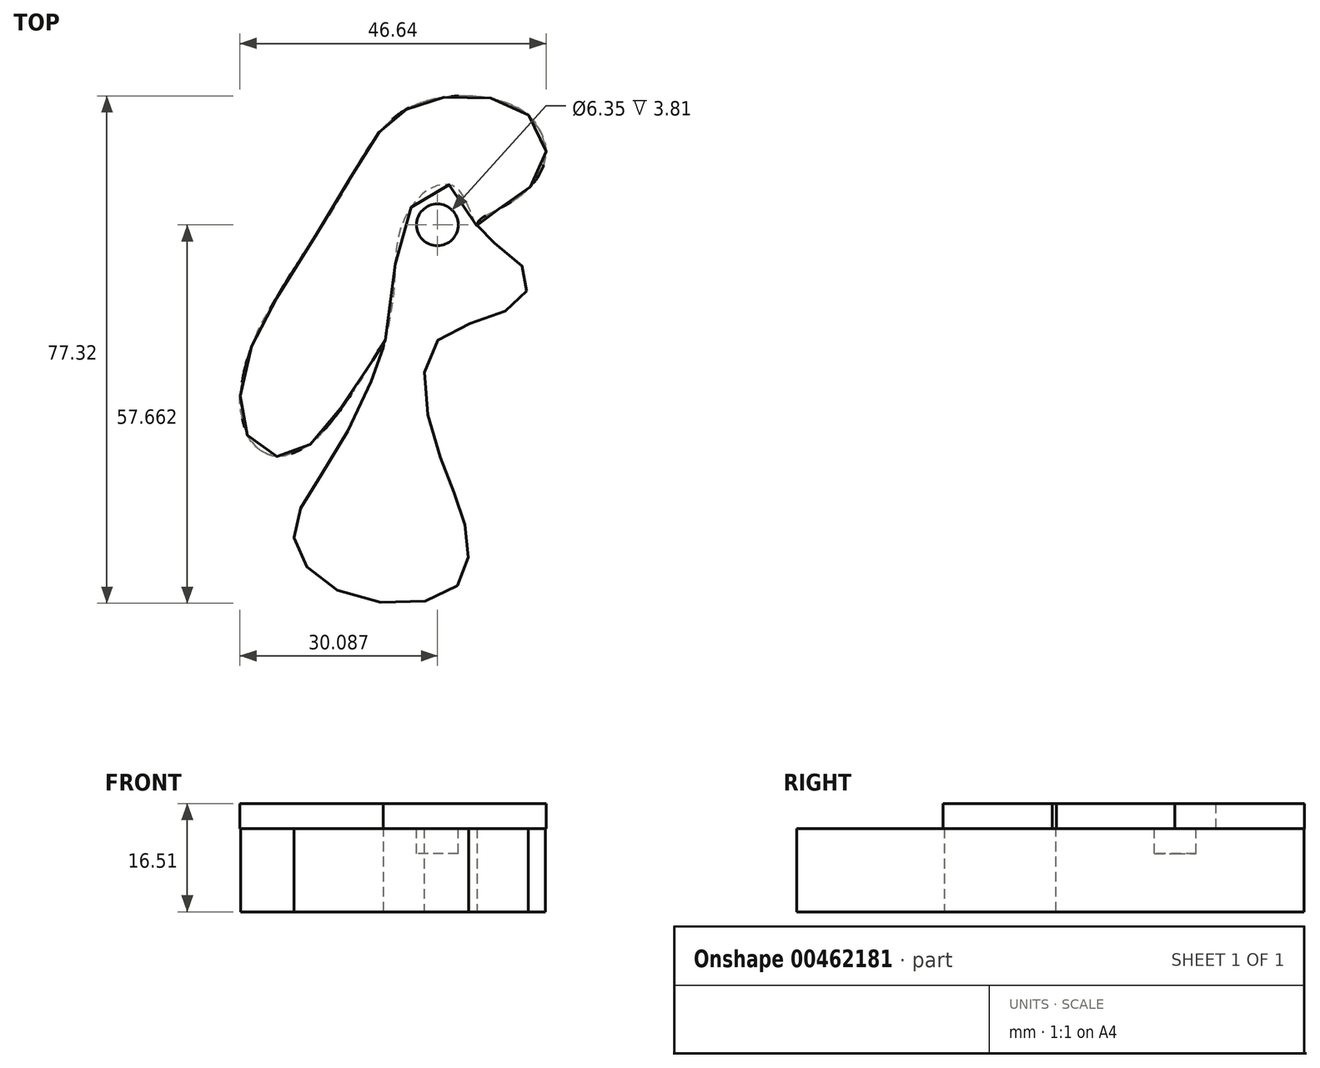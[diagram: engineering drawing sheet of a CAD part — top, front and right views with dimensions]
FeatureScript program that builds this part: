
annotation { "Feature Type Name" : "Feature", "Feature Type Description" : "" }
export const myFeature = defineFeature(function(context is Context, id is Id, definition is map)
    precondition{}
    {
        {
            var Q0;
            Q0=qCreatedBy(makeId("Top.planeOp"),FACE);
            var sketch = newSketch(context, id + "F0", { "sketchPlane" : qUnion([Q0])});
            skFitSpline(sketch, "E0", {"points": [v(0, 0) * mm, v(-6.4, -15.12) * mm, v(-13.6, -28.84) * mm, v(-6.63, -37.68) * mm, v(10.58, -37.45) * mm, v(12.68, -28.6) * mm, v(8.26, -16.05) * mm, v(7.8, 0) * mm, v(19.65, 5.58) * mm, v(21.51, 11.4) * mm, v(14.3, 17.9) * mm, v(18.72, 21.17) * mm, v(24.54, 27.68) * mm, v(21.05, 35.59) * mm, v(4.07, 36.05) * mm, v(-6.86, 21.86) * mm, v(-20.82, -2.8) * mm, v(-19.42, -15.58) * mm, v(-10.82, -14.89) * mm, v(0, 0) * mm]});
            skSolve(sketch);
        }
        {
            var Q0;
            Q0=makeQuery(id+"F0.imprint","IMPRINT",FACE,{"disambiguationData":[TD([[makeQuery(id+"F0.imprint","IMPRINT",EDGE,{"derivedFrom":sQuery(id+"F0.wireOp",EDGE,"E0")}),1.0]])]});
            extrude(context, id + "F1", {"entities" : qUnion([Q0]), "depth" : 12.7 * mm});
        }
        {
            var Q0;
            Q0=makeQuery(id+"F1.opExtrude","CAP_FACE",FACE,{"disambiguationData":[OSD([sQuery(id+"F0.wireOp",EDGE,"E0")])],"isStart":false});
            var sketch = newSketch(context, id + "F2", { "sketchPlane" : qUnion([Q0])});
            skFitSpline(sketch, "E1", {"points": [v(14.59, 18.77) * mm, v(7.56, 24.42) * mm, v(3.14, 23.03) * mm, v(0, 14.42) * mm, v(3.14, 3.95) * mm, v(7.8, 0) * mm, v(9.3, 1.35) * mm, v(15.99, 4) * mm, v(22.1, 9.08) * mm, v(19.49, 13.5) * mm, v(15.67, 16.32) * mm, v(14.59, 18.77) * mm]});
            skCircle(sketch, "E2", {"center": v(8.26, 18.14) * mm, "radius": 3.18 * mm});
            skSolve(sketch);
        }
        {
            var Q0;
            Q0=makeQuery(id+"F2.imprint","IMPRINT",FACE,{"disambiguationData":[TD([[makeQuery(id+"F2.imprint","IMPRINT",EDGE,{"derivedFrom":sQuery(id+"F2.wireOp",EDGE,"E2")}),1.0]])]});
            var Q1;
            Q1=sQuery(id+"F2.wireOp",EDGE,"E2");
            extrude(context, id + "F3", {"entities" : qUnion([Q0]), "operationType" : NewBodyOperationType.REMOVE, "surfaceEntities" : qUnion([Q1]), "oppositeDirection" : true, "depth" : 3.8 * mm});
        }
        {
            var Q0;
            Q0=makeQuery(id+"F1.opExtrude","CAP_FACE",FACE,{"disambiguationData":[OSD([sQuery(id+"F0.wireOp",EDGE,"E0")])],"isStart":false});
            var sketch = newSketch(context, id + "F4", { "sketchPlane" : qUnion([Q0])});
            skSolve(sketch);
        }
        {
            var Q0;
            Q0=makeQuery(id+"F4.imprint","IMPRINT",FACE,{"disambiguationData":[TD([[makeQuery(id+"F4.imprint","IMPRINT",EDGE,{"derivedFrom":makeQuery(id+"F1.opExtrude","CAP_EDGE",EDGE,{"disambiguationData":[OSD([sQuery(id+"F0.wireOp",EDGE,"E0")])],"isStart":false})}),1.0]])]});
            var sketch = newSketch(context, id + "F5", { "sketchPlane" : qUnion([Q0])});
            skFitSpline(sketch, "E3", {"points": [v(14.22, 18.06) * mm, v(11.94, 23.03) * mm, v(8.48, 24.2) * mm, v(5.02, 21.86) * mm, v(2.26, 16.12) * mm, v(1.5, 6.92) * mm, v(0, -0.55) * mm, v(0, 0) * mm, v(-1.48, -2.26) * mm, v(-4.6, -7.24) * mm, v(-8.96, -13.04) * mm, v(-10.93, -15.17) * mm, v(-13.65, -16.57) * mm, v(-15.66, -17.19) * mm, v(-18.25, -16.53) * mm, v(-20.35, -14.56) * mm, v(-21.3, -12.05) * mm, v(-21.83, -8.76) * mm, v(-21.17, -4.44) * mm, v(-19.49, 1.07) * mm, v(-16.75, 6.15) * mm, v(-10.87, 15.55) * mm, v(-6.02, 23.45) * mm, v(-2.78, 29.12) * mm, v(0, 32.93) * mm, v(2.01, 34.73) * mm, v(3.72, 35.86) * mm, v(6.34, 37) * mm, v(9.8, 37.66) * mm, v(14.2, 37.74) * mm, v(18.3, 36.96) * mm, v(21.39, 35.44) * mm, v(23.4, 33.34) * mm, v(24.76, 30.01) * mm, v(24.35, 27.05) * mm, v(22.74, 24.3) * mm, v(20.73, 22.4) * mm, v(17.9, 20.72) * mm, v(15.75, 19.61) * mm, v(14.76, 18.96) * mm, v(14.22, 18.06) * mm]});
            skSolve(sketch);
        }
        {
            var Q0;
            Q0 = qSketchRegion(id + "F5", true);
            var Q1;
            Q1=sQuery(id+"F5.wireOp",EDGE,"E3");
            extrude(context, id + "F6", {"entities" : qUnion([Q0]), "operationType" : NewBodyOperationType.ADD, "surfaceEntities" : qUnion([Q1]), "depth" : 3.8 * mm});
        }
    });
